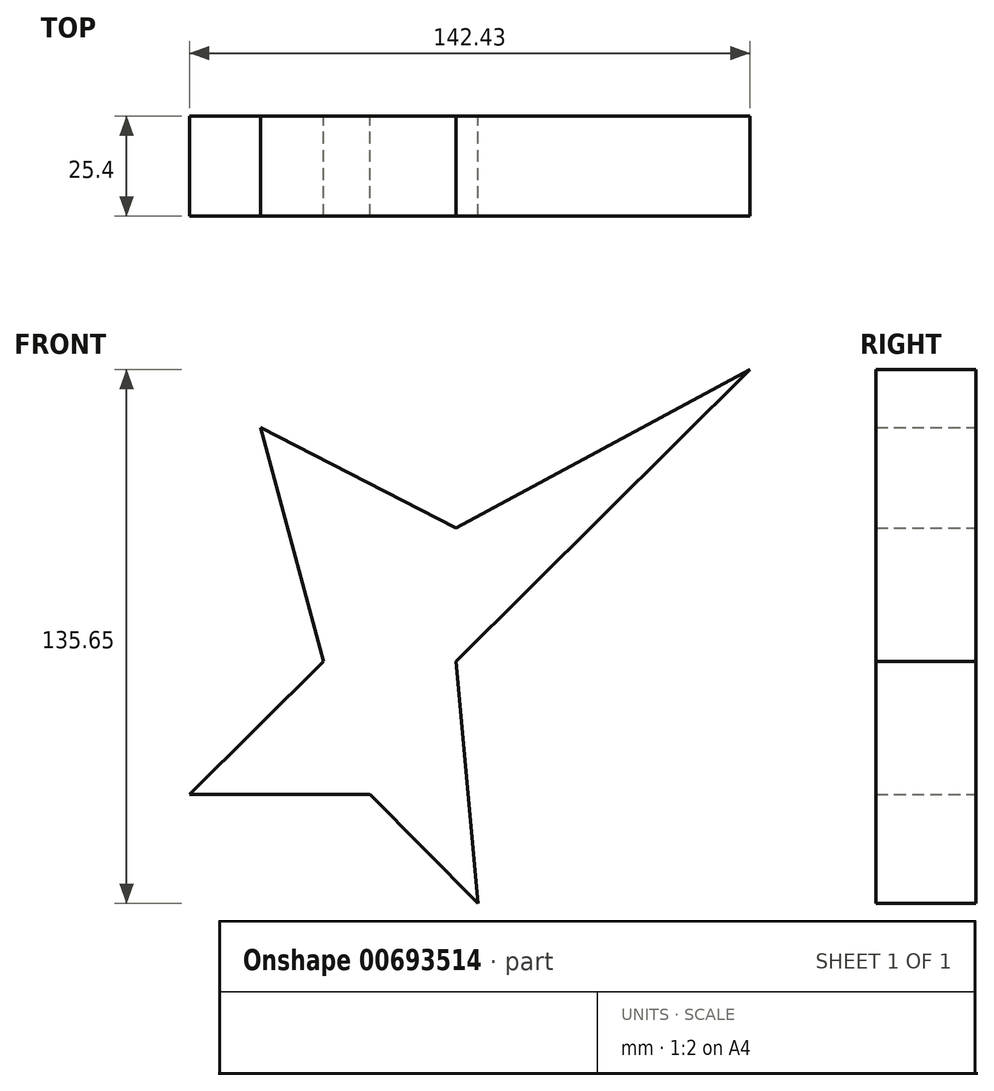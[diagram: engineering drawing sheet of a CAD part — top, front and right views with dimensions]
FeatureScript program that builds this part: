
annotation { "Feature Type Name" : "Feature", "Feature Type Description" : "" }
export const myFeature = defineFeature(function(context is Context, id is Id, definition is map)
    precondition{}
    {
        {
            var Q0;
            Q0=qCreatedBy(makeId("Front.planeOp"),FACE);
            var sketch = newSketch(context, id + "F0", { "sketchPlane" : qUnion([Q0])});
            skLineSegment(sketch, "E0", {"start": v(0, 0) * mm, "end": v(74.68, 74.2) * mm});
            skLineSegment(sketch, "E1", {"start": v(74.68, 74.2) * mm, "end": v(0, 33.9) * mm});
            skLineSegment(sketch, "E2", {"start": v(0, 33.9) * mm, "end": v(-49.74, 59.5) * mm});
            skLineSegment(sketch, "E3", {"start": v(-49.74, 59.5) * mm, "end": v(-33.74, 0) * mm});
            skLineSegment(sketch, "E4", {"start": v(-33.74, 0) * mm, "end": v(-67.75, -33.8) * mm});
            skLineSegment(sketch, "E5", {"start": v(-67.75, -33.8) * mm, "end": v(-21.9, -33.8) * mm});
            skLineSegment(sketch, "E6", {"start": v(-21.9, -33.8) * mm, "end": v(5.57, -61.45) * mm});
            skLineSegment(sketch, "E7", {"start": v(5.57, -61.45) * mm, "end": v(0, 0) * mm});
            skSolve(sketch);
        }
        {
            var Q0;
            Q0=makeQuery(id+"F0.imprint","IMPRINT",FACE,{"disambiguationData":[TD([[makeQuery(id+"F0.imprint","IMPRINT",EDGE,{"derivedFrom":sQuery(id+"F0.wireOp",EDGE,"E0")}),1.0]])]});
            extrude(context, id + "F1", {"entities" : qUnion([Q0]), "depth" : 25.4 * mm, "offsetDistance" : 25.4 * mm});
        }
    });
